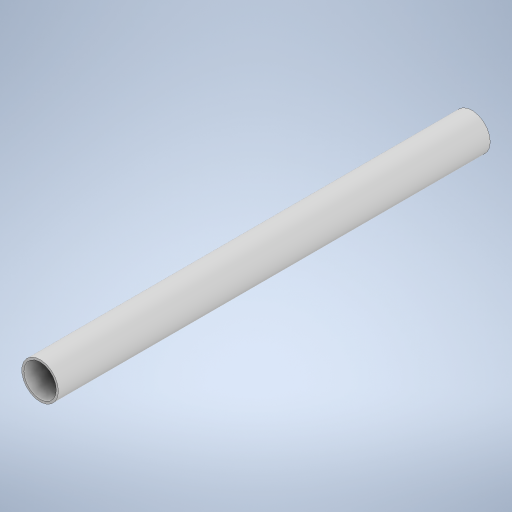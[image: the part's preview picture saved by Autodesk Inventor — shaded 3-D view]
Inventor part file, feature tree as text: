
AUTODESK INVENTOR PART (.ipt)
format: ipt  version: 2023 (Build 270158000, 158)  size: 232,960 bytes
history: native  units: mm
features: extrude x1, sketch x1
ambient origin geometry x8: Origin, YZ Plane, XZ Plane, XY Plane, X Axis, Y Axis, Z Axis, Center Point
bodies: Solido1 (feature_tree)
feature tree (2):
  extrude  "Estrusione1"  Depth=150.0mm
  sketch  "Schizzo1"
